# Revit family: Faucet-Two_Handle-American_Standard-7061857_Series
name_source: partatom
category: Plumbing Fixtures
units: mm (PartAtom-declared; Revit-internal decimal feet)

## family parameters
Always vertical = No
Cut with Voids When Loaded = No
OmniClass Number = 23.45.55.17
OmniClass Title = Mixing Faucets
Part Type = Normal
Room Calculation Point = No
Round Connector Dimension = Use Diameter
Shared = Yes
Work Plane-Based = Yes

## types (3) — shared parameters
ADA Compliant = Yes
ANSI A117.1 = Yes
ASME A112.18.1/CSA B125.1 = Yes
Assembly Code = D2020300
CSA B125.1 = Yes
CW Connection = Yes
CWFU = 1.5
Cold Water Connection Diameter = 3/8"
Cold Water Connection Radius = 3/16"
Default Elevation = 0"
Description = Aspirations™ Widespread Bathroom Faucet with Selectronic® Hands-Free Technology
Drain = Yes
Flow Rate = 1.2 gpm/ 4.5 L/min.
HW Connection = No
HWFU = 1.5
Height = 8 1/4"
Hot Water Connection Diameter = 0"
Hot Water Connection Radius = 3/16"
Installation Type = Deck Mounted
Length = 8"
Manufacturer = American Standard
NSF/ANSI/CAN 372 = Yes
NSF/ANSI/CAN 61 = Yes
Price = Prices may vary. Please consult Manufacturer Representative for most up-to-date price list.
URL = https://www.americanstandard-us.com
Vent Connection = Yes
WFU = 2
Waste Connection = Yes
Waste Connection Diameter = 1 1/4"
Width = 4 13/16"

## per-type parameters (varying)
| type | Drain Depth | Drain Width | Finish | Material |
| 7061857.002 | 7" | 3" | Brass-American Standard-002-Polished Chrome | Brass-American Standard-002-Polished Chrome |
| 7061857.295 | 5 15/16" | 5 15/16" | Brass-American Standard-295-Brushed Nickel | Brass-American Standard-295-Brushed Nickel |
| 7061857.243 | 5 15/16" | 5 15/16" | Brass-American Standard-243-Matte Black | Brass-American Standard-243-Matte Black |

note: column(s) folded — value = type name in every type: Model

## geometry (parser evidence)
native form markers: Sweep x5
no freeform markers — native parametric forms only
